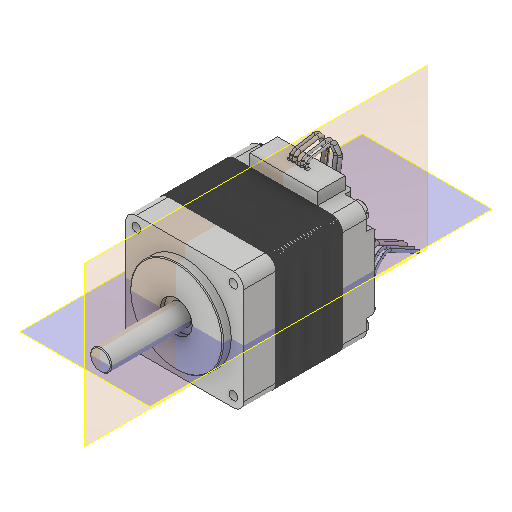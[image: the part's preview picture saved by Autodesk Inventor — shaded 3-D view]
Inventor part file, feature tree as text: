
AUTODESK INVENTOR PART (.ipt)
format: ipt  version: 2024.1 (Build 281209000, 209)  size: 3,377,152 bytes
history: native  units: mm
features: other x8, plane x2
ambient origin geometry x8: Origin, YZ Plane, XZ Plane, XY Plane, X Axis, Y Axis, Z Axis, Center Point
bodies: Solid1 (feature_tree), Solid2 (feature_tree), Solid3 (feature_tree), Solid4 (feature_tree), Solid5 (feature_tree), Solid6 (feature_tree), Solid7 (feature_tree), Solid8 (feature_tree)
feature tree (10):
  plane  "Work Plane1"
  plane  "Arbeitsebene2"
  other  "Lagerschild_11_1:1"
  other  "Welle_11_2:1"
  other  "Kollektorschild_11_3:1"
  other  "Schraube_M2x25_4:1"
  other  "Schraube_M2x25_5:1"
  other  "Schraube_M2x25_6:1"
  other  "Schraube_M2x25_7:1"
  other  "Stator_11_8:1"
